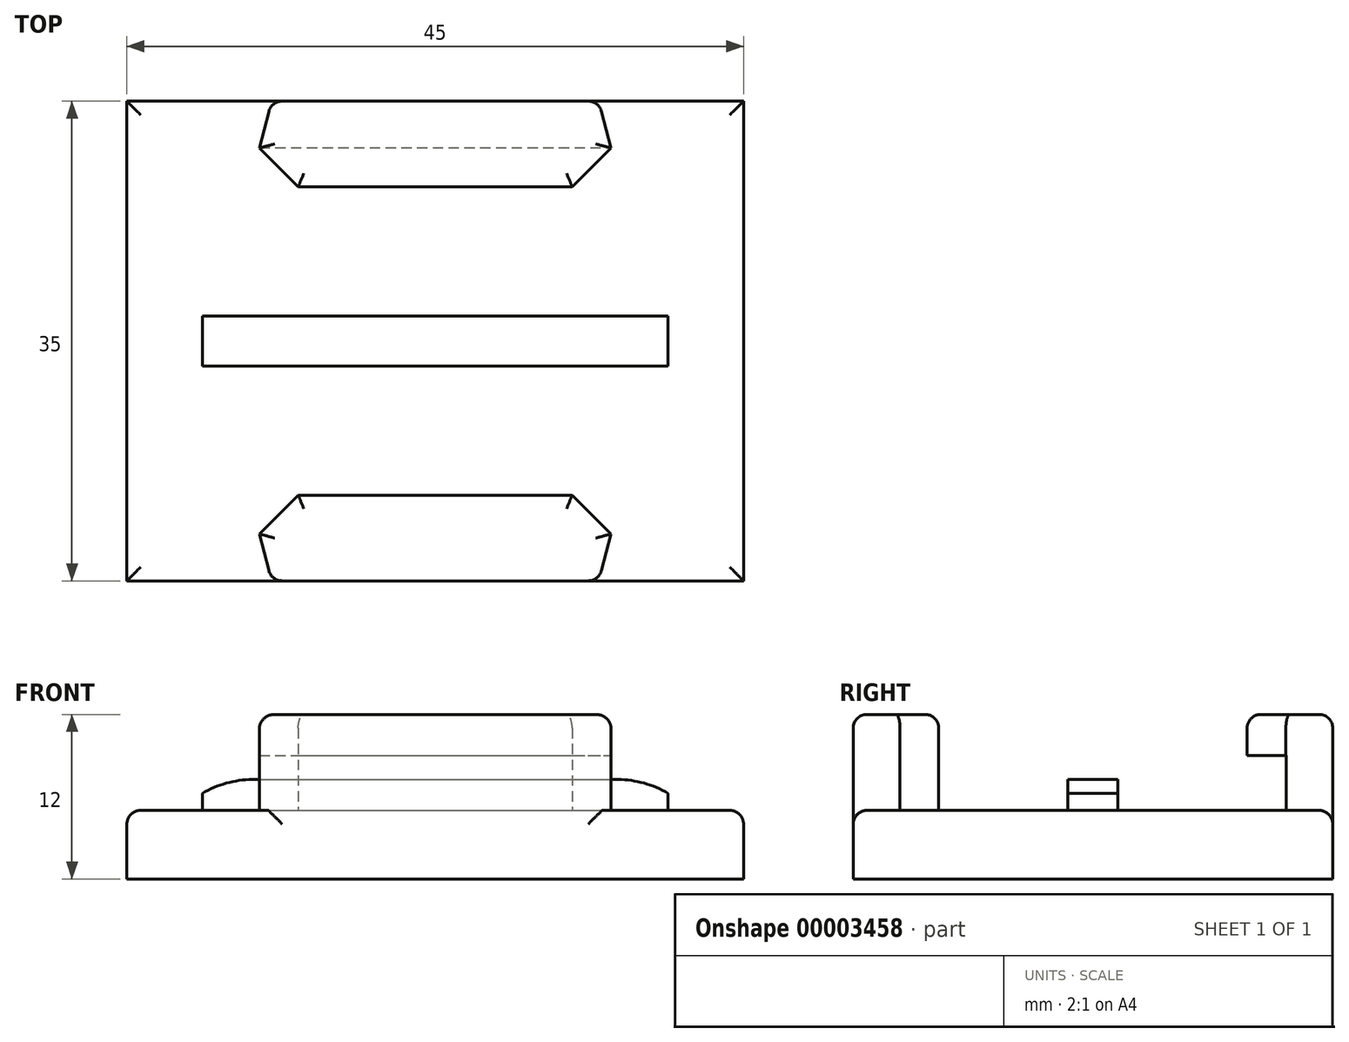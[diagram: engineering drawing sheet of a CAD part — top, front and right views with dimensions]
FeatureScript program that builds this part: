
annotation { "Feature Type Name" : "Feature", "Feature Type Description" : "" }
export const myFeature = defineFeature(function(context is Context, id is Id, definition is map)
    precondition{}
    {
        {
            var Q0;
            Q0=qCreatedBy(makeId("Top.planeOp"),FACE);
            var sketch = newSketch(context, id + "F0", { "sketchPlane" : qUnion([Q0])});
            skLineSegment(sketch, "E0.rect.bottom", {"start": v(-22.5, 17.5) * mm, "end": v(22.5, 17.5) * mm});
            skLineSegment(sketch, "E0.rect.top", {"start": v(-22.5, -17.5) * mm, "end": v(22.5, -17.5) * mm});
            skLineSegment(sketch, "E0.rect.left", {"start": v(-22.5, 17.5) * mm, "end": v(-22.5, -17.5) * mm});
            skLineSegment(sketch, "E0.rect.right", {"start": v(22.5, 17.5) * mm, "end": v(22.5, -17.5) * mm});
            skPoint(sketch, "E0.rect.middle", {"position": v(0, 0) * mm});
            skSolve(sketch);
        }
        {
            var Q0;
            Q0=makeQuery(id+"F0.imprint","IMPRINT",FACE,{"disambiguationData":[TD([[makeQuery(id+"F0.imprint","IMPRINT",EDGE,{"derivedFrom":sQuery(id+"F0.wireOp",EDGE,"E0.rect.bottom")}),-1.0]])]});
            extrude(context, id + "F1", {"entities" : qUnion([Q0]), "depth" : 5 * mm});
        }
        {
            var Q0;
            Q0=makeQuery(id+"F1.opExtrude","CAP_FACE",FACE,{"disambiguationData":[OSD([sQuery(id+"F0.wireOp",EDGE,"E0.rect.bottom"),sQuery(id+"F0.wireOp",EDGE,"E0.rect.top"),sQuery(id+"F0.wireOp",EDGE,"E0.rect.left"),sQuery(id+"F0.wireOp",EDGE,"E0.rect.right")])],"isStart":false});
            var sketch = newSketch(context, id + "F2", { "sketchPlane" : qUnion([Q0])});
            skLineSegment(sketch, "E1.rect.bottom", {"start": v(-17, 1.82) * mm, "end": v(17, 1.82) * mm});
            skLineSegment(sketch, "E1.rect.top", {"start": v(-17, -1.83) * mm, "end": v(17, -1.83) * mm});
            skLineSegment(sketch, "E1.rect.left", {"start": v(-17, 1.82) * mm, "end": v(-17, -1.83) * mm});
            skLineSegment(sketch, "E1.rect.right", {"start": v(17, 1.82) * mm, "end": v(17, -1.83) * mm});
            skPoint(sketch, "E1.rect.middle", {"position": v(0, 0) * mm});
            skSolve(sketch);
        }
        {
            var Q0;
            Q0=makeQuery(id+"F2.imprint","IMPRINT",FACE,{"disambiguationData":[TD([[makeQuery(id+"F2.imprint","IMPRINT",EDGE,{"derivedFrom":sQuery(id+"F2.wireOp",EDGE,"E1.rect.bottom")}),-1.0]])]});
            extrude(context, id + "F3", {"entities" : qUnion([Q0]), "operationType" : NewBodyOperationType.ADD, "depth" : 2.25 * mm});
        }
        {
            var Q0;
            Q0=makeQuery(id+"F3.opExtrude","SWEPT_FACE",FACE,{"disambiguationData":[OSD([sQuery(id+"F2.wireOp",EDGE,"E1.rect.top")])]});
            var sketch = newSketch(context, id + "F4", { "sketchPlane" : qUnion([Q0])});
            skLineSegment(sketch, "E2", {"start": v(-17, 7.25) * mm, "end": v(17, 7.25) * mm, "construction": true});
            skLineSegment(sketch, "E3.0", {"start": v(-17, 6.25) * mm, "end": v(17, 6.25) * mm});
            skArc(sketch, "E4", {"start": v(-13.26, 7.25) * mm, "mid": v(-15.2, 7) * mm, "end": v(-17, 6.25) * mm});
            skLineSegment(sketch, "E5", {"start": v(0, 0) * mm, "end": v(0, 15.47) * mm, "construction": true});
            skArc(sketch, "E6.0.MirrorCS", {"start": v(13.26, 7.25) * mm, "mid": v(15.2, 7) * mm, "end": v(17, 6.25) * mm});
            skLineSegment(sketch, "E7", {"start": v(-17, 6.25) * mm, "end": v(-18.16, 6.25) * mm});
            skLineSegment(sketch, "E8", {"start": v(-18.16, 6.25) * mm, "end": v(-18.16, 8.7) * mm});
            skLineSegment(sketch, "E9", {"start": v(-18.16, 8.7) * mm, "end": v(-13.25, 8.7) * mm});
            skLineSegment(sketch, "E10", {"start": v(-13.25, 8.7) * mm, "end": v(-13.26, 7.25) * mm});
            skLineSegment(sketch, "E11", {"start": v(13.26, 7.25) * mm, "end": v(13.26, 8.4) * mm});
            skLineSegment(sketch, "E12", {"start": v(13.26, 8.4) * mm, "end": v(18.11, 8.4) * mm});
            skLineSegment(sketch, "E13", {"start": v(18.11, 8.4) * mm, "end": v(18.11, 6.28) * mm});
            skLineSegment(sketch, "E14", {"start": v(18.11, 6.28) * mm, "end": v(17, 6.25) * mm});
            skSolve(sketch);
        }
        {
            var Q0;
            {var subQ0=sQuery(id+"F2.wireOp",EDGE,"E1.rect.top");var subQ1=makeQuery(id+"F3.opExtrude","CAP_EDGE",EDGE,{"disambiguationData":[OSD([subQ0])],"isStart":false});var subQ2=sQuery(id+"F4.wireOp",EDGE,"E4");var subQ3=makeQuery(id+"F4.imprint","INTERSECT",VERTEX,{"derivedFrom":[subQ1,subQ2]});var subQ6=makeQuery(id+"F4.imprint","IMPRINT",EDGE,{"disambiguationData":[TD([[subQ3,1.0]])],"derivedFrom":subQ1});var subQ8=sQuery(id+"F4.wireOp",EDGE,"E7");var subQ13=sQuery(id+"F4.wireOp",EDGE,"E6.0.MirrorCS");var subQ18=makeQuery(id+"F4.imprint","INTERSECT",VERTEX,{"derivedFrom":[subQ1,subQ13]});var subQ19=makeQuery(id+"F4.imprint","IMPRINT",EDGE,{"disambiguationData":[TD([[subQ18,-1.0]])],"derivedFrom":subQ1});var subQ20=sQuery(id+"F4.wireOp",EDGE,"E11");Q0=qUnion([makeQuery(id+"F4.imprint","IMPRINT",FACE,{"disambiguationData":[TD([[makeQuery(id+"F4.imprint","IMPRINT",EDGE,{"derivedFrom":subQ8}),-1.0]])]}),makeQuery(id+"F4.imprint","IMPRINT",FACE,{"disambiguationData":[TD([[subQ6,-1.0]])]}),makeQuery(id+"F4.imprint","IMPRINT",FACE,{"disambiguationData":[TD([[makeQuery(id+"F4.imprint","IMPRINT",EDGE,{"derivedFrom":subQ20}),-1.0]])]}),makeQuery(id+"F4.imprint","IMPRINT",FACE,{"disambiguationData":[TD([[subQ19,-1.0]])]})]);}
            extrude(context, id + "F5", {"entities" : qUnion([Q0]), "operationType" : NewBodyOperationType.REMOVE, "endBound" : BoundingType.THROUGH_ALL, "oppositeDirection" : true, "depth" : 25 * mm});
        }
        {
            var Q0;
            Q0=makeQuery(id+"F1.opExtrude","CAP_FACE",FACE,{"disambiguationData":[OSD([sQuery(id+"F0.wireOp",EDGE,"E0.rect.bottom"),sQuery(id+"F0.wireOp",EDGE,"E0.rect.top"),sQuery(id+"F0.wireOp",EDGE,"E0.rect.left"),sQuery(id+"F0.wireOp",EDGE,"E0.rect.right")])],"isStart":false});
            var sketch = newSketch(context, id + "F6", { "sketchPlane" : qUnion([Q0])});
            skLineSegment(sketch, "E15.rect.bottom", {"start": v(-11.94, 17.5) * mm, "end": v(11.94, 17.5) * mm, "construction": true});
            skPoint(sketch, "E15.rect.middle", {"position": v(0, 0) * mm});
            skLineSegment(sketch, "E16.0", {"start": v(-10, 11.25) * mm, "end": v(10, 11.25) * mm});
            skLineSegment(sketch, "E17", {"start": v(-10, 11.25) * mm, "end": v(-12.82, 14.08) * mm, "construction": true});
            skLineSegment(sketch, "E18.0.MirrorCS", {"start": v(10, 11.25) * mm, "end": v(12.82, 14.08) * mm, "construction": true});
            skLineSegment(sketch, "E19", {"start": v(10, 11.25) * mm, "end": v(12.82, 14.08) * mm});
            skLineSegment(sketch, "E20", {"start": v(11.94, 17.5) * mm, "end": v(-11.94, 17.5) * mm});
            skLineSegment(sketch, "E21", {"start": v(-12.82, 14.08) * mm, "end": v(-10, 11.25) * mm});
            skLineSegment(sketch, "E22.0.MirrorCS", {"start": v(-10, -11.25) * mm, "end": v(-12.82, -14.08) * mm, "construction": true});
            skLineSegment(sketch, "E22.1.MirrorCS", {"start": v(-11.94, -17.5) * mm, "end": v(11.94, -17.5) * mm, "construction": true});
            skLineSegment(sketch, "E22.2.MirrorCS", {"start": v(-11.94, -17.5) * mm, "end": v(11.94, -17.5) * mm, "construction": true});
            skLineSegment(sketch, "E22.4.MirrorCS", {"start": v(-10, -11.25) * mm, "end": v(-12.82, -14.08) * mm, "construction": true});
            skLineSegment(sketch, "E22.5.MirrorCS", {"start": v(10, -11.25) * mm, "end": v(12.82, -14.08) * mm, "construction": true});
            skLineSegment(sketch, "E22.7.MirrorCS", {"start": v(11.94, -17.5) * mm, "end": v(-11.94, -17.5) * mm});
            skLineSegment(sketch, "E22.9.MirrorCS", {"start": v(10, -11.25) * mm, "end": v(12.82, -14.08) * mm});
            skLineSegment(sketch, "E22.10.MirrorCS", {"start": v(-12.82, -14.08) * mm, "end": v(-10, -11.25) * mm});
            skLineSegment(sketch, "E22.12.MirrorCS", {"start": v(-10, -11.25) * mm, "end": v(10, -11.25) * mm});
            skLineSegment(sketch, "E23", {"start": v(12.82, 14.08) * mm, "end": v(11.94, 17.5) * mm});
            skLineSegment(sketch, "E24.0.MirrorCS", {"start": v(12.82, -14.08) * mm, "end": v(11.94, -17.5) * mm});
            skLineSegment(sketch, "E25.0.MirrorCS", {"start": v(-12.82, 14.08) * mm, "end": v(-11.94, 17.5) * mm});
            skLineSegment(sketch, "E26.0.MirrorCS", {"start": v(-12.82, -14.08) * mm, "end": v(-11.94, -17.5) * mm});
            skSolve(sketch);
        }
        {
            var Q0;
            {Q0=qUnion([makeQuery(id+"F6.imprint","IMPRINT",FACE,{"disambiguationData":[TD([[makeQuery(id+"F6.imprint","IMPRINT",EDGE,{"derivedFrom":sQuery(id+"F6.wireOp",EDGE,"E16.0")}),1.0]])]}),makeQuery(id+"F6.imprint","IMPRINT",FACE,{"disambiguationData":[TD([[makeQuery(id+"F6.imprint","IMPRINT",EDGE,{"derivedFrom":sQuery(id+"F6.wireOp",EDGE,"E22.7.MirrorCS")}),1.0]])]})]);}
            extrude(context, id + "F7", {"entities" : qUnion([Q0]), "operationType" : NewBodyOperationType.ADD, "depth" : 7 * mm});
        }
        {
            var Q0;
            Q0=qCreatedBy(makeId("Right.planeOp"),FACE);
            var sketch = newSketch(context, id + "F8", { "sketchPlane" : qUnion([Q0])});
            skLineSegment(sketch, "E27.0", {"start": v(14.1, 9) * mm, "end": v(14.1, 5) * mm});
            skLineSegment(sketch, "E28.bottom", {"start": v(14.1, 5) * mm, "end": v(10.15, 5) * mm});
            skLineSegment(sketch, "E28.top", {"start": v(14.1, 9) * mm, "end": v(10.15, 9) * mm});
            skLineSegment(sketch, "E28.left", {"start": v(14.1, 5) * mm, "end": v(14.1, 9) * mm});
            skLineSegment(sketch, "E28.right", {"start": v(10.15, 5) * mm, "end": v(10.15, 9) * mm});
            skLineSegment(sketch, "E29.0.MirrorCS", {"start": v(-14.1, 5) * mm, "end": v(-14.1, 9) * mm});
            skLineSegment(sketch, "E29.1.MirrorCS", {"start": v(-14.1, 9) * mm, "end": v(-14.1, 5) * mm});
            skLineSegment(sketch, "E29.2.MirrorCS", {"start": v(-14.1, 9) * mm, "end": v(-10.15, 9) * mm});
            skLineSegment(sketch, "E29.3.MirrorCS", {"start": v(-10.15, 5) * mm, "end": v(-10.15, 9) * mm});
            skLineSegment(sketch, "E29.4.MirrorCS", {"start": v(-14.1, 5) * mm, "end": v(-10.15, 5) * mm});
            skSolve(sketch);
        }
        {
            var Q0;
            {Q0=qUnion([makeQuery(id+"F8.imprint","IMPRINT",FACE,{"disambiguationData":[TD([[makeQuery(id+"F8.imprint","IMPRINT",EDGE,{"derivedFrom":sQuery(id+"F8.wireOp",EDGE,"E28.bottom")}),-1.0]])]}),makeQuery(id+"F8.imprint","IMPRINT",FACE,{"disambiguationData":[TD([[makeQuery(id+"F8.imprint","IMPRINT",EDGE,{"derivedFrom":sQuery(id+"F8.wireOp",EDGE,"E29.1.MirrorCS")}),1.0]])]})]);}
            extrude(context, id + "F9", {"entities" : qUnion([Q0]), "operationType" : NewBodyOperationType.REMOVE, "oppositeDirection" : true, "depth" : 31.01 * mm, "symmetric" : true});
        }
        {
            var Q0;
            Q0=makeQuery(id+"F7.opExtrude","CAP_FACE",FACE,{"disambiguationData":[OSD([sQuery(id+"F6.wireOp",EDGE,"E16.0"),sQuery(id+"F6.wireOp",EDGE,"E19"),sQuery(id+"F6.wireOp",EDGE,"E20"),sQuery(id+"F6.wireOp",EDGE,"E21"),sQuery(id+"F6.wireOp",EDGE,"E23"),sQuery(id+"F6.wireOp",EDGE,"E25.0.MirrorCS")])],"isStart":false});
            var Q1;
            Q1=makeQuery(id+"F7.opExtrude","CAP_FACE",FACE,{"disambiguationData":[OSD([sQuery(id+"F6.wireOp",EDGE,"E22.7.MirrorCS"),sQuery(id+"F6.wireOp",EDGE,"E22.9.MirrorCS"),sQuery(id+"F6.wireOp",EDGE,"E22.10.MirrorCS"),sQuery(id+"F6.wireOp",EDGE,"E22.12.MirrorCS"),sQuery(id+"F6.wireOp",EDGE,"E24.0.MirrorCS"),sQuery(id+"F6.wireOp",EDGE,"E26.0.MirrorCS")])],"isStart":false});
            var Q2;
            Q2=makeQuery(id+"F7.opExtrude","SWEPT_EDGE",EDGE,{"disambiguationData":[OSD([sQuery(id+"F0.wireOp",EDGE,"E0.rect.bottom"),sQuery(id+"F6.wireOp",EDGE,"E20"),sQuery(id+"F6.wireOp",EDGE,"E23")])]});
            var Q3;
            Q3=makeQuery(id+"F7.opExtrude","SWEPT_EDGE",EDGE,{"disambiguationData":[OSD([sQuery(id+"F0.wireOp",EDGE,"E0.rect.bottom"),sQuery(id+"F6.wireOp",EDGE,"E20"),sQuery(id+"F6.wireOp",EDGE,"E25.0.MirrorCS")])]});
            var Q4;
            Q4=makeQuery(id+"F7.opExtrude","SWEPT_EDGE",EDGE,{"disambiguationData":[OSD([sQuery(id+"F0.wireOp",EDGE,"E0.rect.top"),sQuery(id+"F6.wireOp",EDGE,"E22.7.MirrorCS"),sQuery(id+"F6.wireOp",EDGE,"E24.0.MirrorCS")])]});
            var Q5;
            Q5=makeQuery(id+"F7.opExtrude","SWEPT_EDGE",EDGE,{"disambiguationData":[OSD([sQuery(id+"F0.wireOp",EDGE,"E0.rect.top"),sQuery(id+"F6.wireOp",EDGE,"E22.7.MirrorCS"),sQuery(id+"F6.wireOp",EDGE,"E26.0.MirrorCS")])]});
            fillet(context, id + "F10", {"entities" : qUnion([Q0, Q1, Q2, Q3, Q4, Q5]), "radius" : 1 * mm, "tangentPropagation" : true, "allowEdgeOverflow" : false});
        }
        {
            var Q0;
            {var subQ0=sQuery(id+"F0.wireOp",EDGE,"E0.rect.top");var subQ1=sQuery(id+"F0.wireOp",EDGE,"E0.rect.right");Q0=makeQuery(id+"F7.boolean.opBoolean","SPLIT",EDGE,{"disambiguationData":[TD([makeQuery(id+"F1.opExtrude","SWEPT_FACE",FACE,{"disambiguationData":[OSD([subQ1])]})])],"derivedFrom":makeQuery(id+"F1.opExtrude","CAP_EDGE",EDGE,{"disambiguationData":[OSD([subQ0])],"isStart":false})});}
            var Q1;
            Q1=makeQuery(id+"F1.opExtrude","CAP_EDGE",EDGE,{"disambiguationData":[OSD([sQuery(id+"F0.wireOp",EDGE,"E0.rect.right")])],"isStart":false});
            var Q2;
            {var subQ0=sQuery(id+"F0.wireOp",EDGE,"E0.rect.bottom");var subQ1=sQuery(id+"F0.wireOp",EDGE,"E0.rect.right");Q2=makeQuery(id+"F7.boolean.opBoolean","SPLIT",EDGE,{"disambiguationData":[TD([makeQuery(id+"F1.opExtrude","SWEPT_FACE",FACE,{"disambiguationData":[OSD([subQ1])]})])],"derivedFrom":makeQuery(id+"F1.opExtrude","CAP_EDGE",EDGE,{"disambiguationData":[OSD([subQ0])],"isStart":false})});}
            var Q3;
            {var subQ0=sQuery(id+"F0.wireOp",EDGE,"E0.rect.bottom");var subQ1=sQuery(id+"F0.wireOp",EDGE,"E0.rect.left");Q3=makeQuery(id+"F7.boolean.opBoolean","SPLIT",EDGE,{"disambiguationData":[TD([makeQuery(id+"F1.opExtrude","SWEPT_FACE",FACE,{"disambiguationData":[OSD([subQ1])]})])],"derivedFrom":makeQuery(id+"F1.opExtrude","CAP_EDGE",EDGE,{"disambiguationData":[OSD([subQ0])],"isStart":false})});}
            var Q4;
            Q4=makeQuery(id+"F1.opExtrude","CAP_EDGE",EDGE,{"disambiguationData":[OSD([sQuery(id+"F0.wireOp",EDGE,"E0.rect.left")])],"isStart":false});
            var Q5;
            {var subQ0=sQuery(id+"F0.wireOp",EDGE,"E0.rect.top");var subQ1=sQuery(id+"F0.wireOp",EDGE,"E0.rect.left");Q5=makeQuery(id+"F7.boolean.opBoolean","SPLIT",EDGE,{"disambiguationData":[TD([makeQuery(id+"F1.opExtrude","SWEPT_FACE",FACE,{"disambiguationData":[OSD([subQ1])]})])],"derivedFrom":makeQuery(id+"F1.opExtrude","CAP_EDGE",EDGE,{"disambiguationData":[OSD([subQ0])],"isStart":false})});}
            fillet(context, id + "F11", {"entities" : qUnion([Q0, Q1, Q2, Q3, Q4, Q5]), "radius" : 1 * mm, "allowEdgeOverflow" : false});
        }
    });
